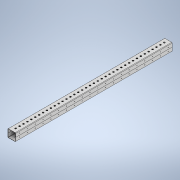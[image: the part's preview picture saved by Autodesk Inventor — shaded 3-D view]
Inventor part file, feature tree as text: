
AUTODESK INVENTOR PART (.ipt)
format: ipt  version: 2022 (Build 260153000, 153)  size: 398,336 bytes
history: native  units: mm
features: sheet_metal_op x4, sketch x4, extrude x3, pattern_linear x3, other x3, mirror x1, move_body x1
ambient origin geometry x8: Origin, YZ Plane, XZ Plane, XY Plane, X Axis, Y Axis, Z Axis, Center Point
bodies: Solid1 (feature_tree), Solid2 (feature_tree)
feature tree (19):
  sheet_metal_op  "Face1"
  sheet_metal_op  "Flange1"
  extrude  "Extrusion2"  Depth=1000.0mm
  pattern_linear  "Rectangular Pattern3"  Spacing1=25.0mm  [1 undecoded]
  sketch  "Sketch9"  dims[d3=10.1mm]
  sketch  "Sketch10"  dims[d4=25.0mm d5=25.0mm d21=1.5mm d22=0.0mm d29=20.0mm d31=0.0mm d32=390.0mm d34=25.0mm d36=1.5mm d37=0.75mm d38=3.0mm d39=1.5mm d40=25.0mm d41=90.0deg d42=1.5mm d43=6.0mm d44=1.5mm d45=1.5mm d56=0.0mm d57=50.0mm d58=0.0mm d91=25.0mm d92=3.335mm d93=22.0mm d94=11.0mm d95=25.0mm d96=2.0mm d97=0.0mm d98=10.0mm d100=10.0mm d101=200.0mm d103=50.0mm d104=3.35mm d105=25.0mm d106=11.0mm d107=2.0mm d108=0.0mm d109=10.0mm d111=10.0mm d112=200.0mm d114=50.0mm]
  extrude  "Extrusion6"  Depth=1.5mm TaperAngle=0.0deg
  extrude  "Extrusion7"  Depth=25.0mm TaperAngle=0.0deg
  pattern_linear  "Rectangular Pattern5"  Spacing1=1.5mm  [1 undecoded]
  pattern_linear  "Rectangular Pattern6"  Spacing1=0.75mm  [1 undecoded]
  mirror  "Mirror1"
  move_body  "Move Body1"
  other  "Plate1"
  sketch  "Sketch2"  dims[d0=50.0mm d1=1000.0mm]
  sketch  "Sketch3"  dims[d2=1.5mm]
  other  "Plate2"
  sheet_metal_op  "Bend1"
  sheet_metal_op  "Corner1"
  other  "Pattern of Solid1:1"
note: 3 required parameter values undecoded (feature->parameter linkage not recoverable at this tier; creation-order binding heuristic only, values carry confidence <= 0.55)
